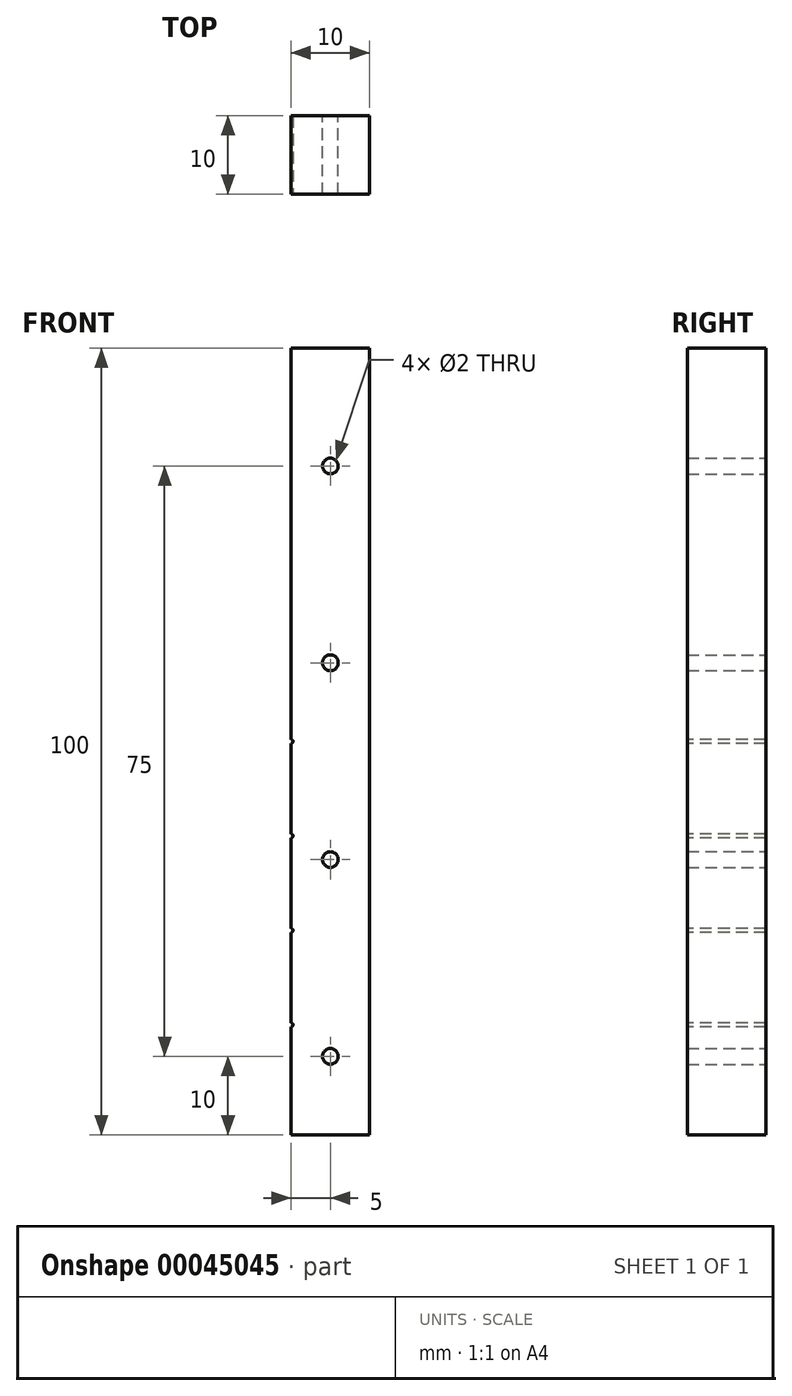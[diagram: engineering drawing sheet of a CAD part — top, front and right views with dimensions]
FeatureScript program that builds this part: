
annotation { "Feature Type Name" : "Feature", "Feature Type Description" : "" }
export const myFeature = defineFeature(function(context is Context, id is Id, definition is map)
    precondition{}
    {
        {
            var Q0;
            Q0=qCreatedBy(makeId("Front.planeOp"),FACE);
            var sketch = newSketch(context, id + "F0", { "sketchPlane" : qUnion([Q0])});
            skLineSegment(sketch, "E0.bottom", {"start": v(0, 0) * mm, "end": v(10, 0) * mm});
            skLineSegment(sketch, "E0.top", {"start": v(0, 100) * mm, "end": v(10, 100) * mm});
            skLineSegment(sketch, "E0.left", {"start": v(0, 0) * mm, "end": v(0, 100) * mm});
            skLineSegment(sketch, "E0.right", {"start": v(10, 0) * mm, "end": v(10, 100) * mm});
            skSolve(sketch);
        }
        {
            var Q0;
            Q0 = qSketchRegion(id + "F0", true);
            extrude(context, id + "F1", {"entities" : qUnion([Q0]), "depth" : 10 * mm});
        }
        {
            var Q0;
            Q0=makeQuery(id+"F1.opExtrude","CAP_FACE",FACE,{"disambiguationData":[OSD([sQuery(id+"F0.wireOp",EDGE,"E0.bottom"),sQuery(id+"F0.wireOp",EDGE,"E0.top"),sQuery(id+"F0.wireOp",EDGE,"E0.left"),sQuery(id+"F0.wireOp",EDGE,"E0.right")])],"isStart":false});
            var sketch = newSketch(context, id + "F2", { "sketchPlane" : qUnion([Q0])});
            skCircle(sketch, "E1", {"center": v(0, 50) * mm, "radius": 0.25 * mm});
            skCircle(sketch, "E2.0.1.0", {"center": v(0, 38) * mm, "radius": 0.25 * mm});
            skCircle(sketch, "E2.0.2.0", {"center": v(0, 26) * mm, "radius": 0.25 * mm});
            skCircle(sketch, "E2.0.3.0", {"center": v(0, 14) * mm, "radius": 0.25 * mm});
            skLineSegment(sketch, "E2.direction1", {"start": v(0, 50) * mm, "end": v(24.94, 50) * mm, "construction": true});
            skLineSegment(sketch, "E2.direction2", {"start": v(0, 50) * mm, "end": v(0, 38) * mm, "construction": true});
            skSolve(sketch);
        }
        {
            var Q0;
            Q0 = qSketchRegion(id + "F2", true);
            extrude(context, id + "F3", {"entities" : qUnion([Q0]), "operationType" : NewBodyOperationType.REMOVE, "endBound" : BoundingType.THROUGH_ALL, "oppositeDirection" : true, "depth" : 25 * mm});
        }
        {
            var Q0;
            Q0=qCreatedBy(makeId("Front.planeOp"),FACE);
            var sketch = newSketch(context, id + "F4", { "sketchPlane" : qUnion([Q0])});
            skLineSegment(sketch, "E3", {"start": v(5, 0) * mm, "end": v(5, 104.48) * mm, "construction": true});
            skCircle(sketch, "E4", {"center": v(5, 85) * mm, "radius": 1 * mm});
            skCircle(sketch, "E5.0.1.0", {"center": v(5, 60) * mm, "radius": 1 * mm});
            skCircle(sketch, "E5.0.2.0", {"center": v(5, 35) * mm, "radius": 1 * mm});
            skCircle(sketch, "E5.0.3.0", {"center": v(5, 10) * mm, "radius": 1 * mm});
            skLineSegment(sketch, "E5.direction1", {"start": v(5, 85) * mm, "end": v(30, 85) * mm, "construction": true});
            skLineSegment(sketch, "E5.direction2", {"start": v(5, 85) * mm, "end": v(5, 60) * mm, "construction": true});
            skSolve(sketch);
        }
        {
            var Q0;
            Q0 = qSketchRegion(id + "F4", true);
            extrude(context, id + "F5", {"entities" : qUnion([Q0]), "operationType" : NewBodyOperationType.REMOVE, "endBound" : BoundingType.THROUGH_ALL, "depth" : 25 * mm});
        }
    });
